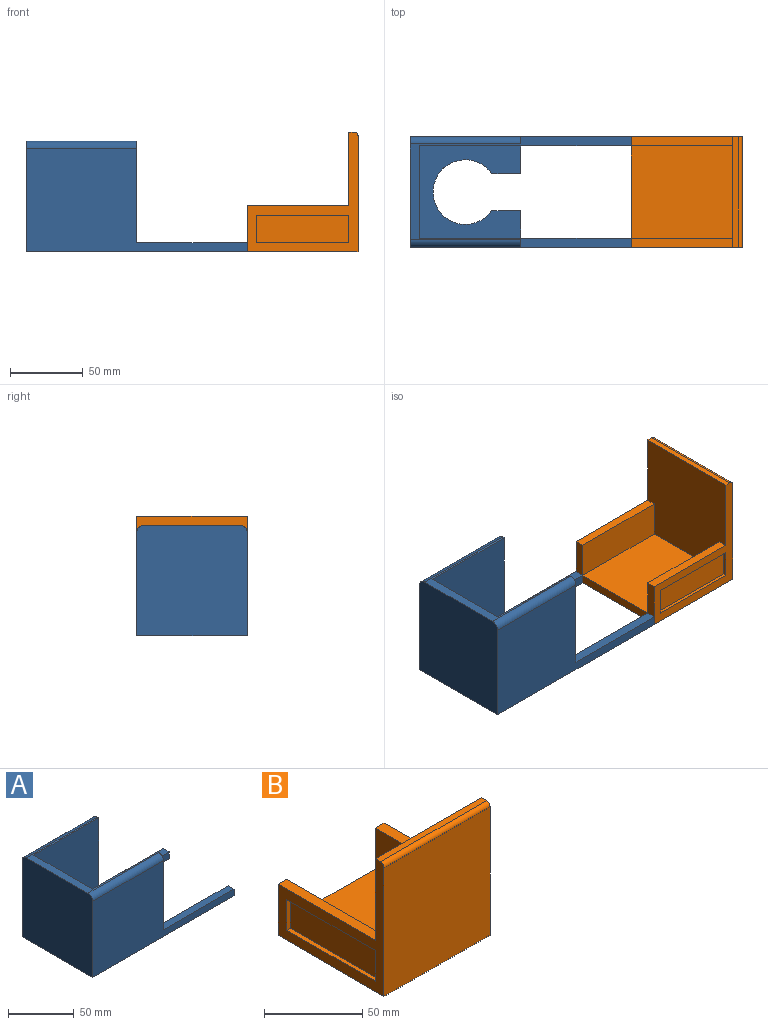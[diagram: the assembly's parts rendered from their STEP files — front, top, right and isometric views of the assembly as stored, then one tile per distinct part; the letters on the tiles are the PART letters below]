
ASSEMBLY  parts=2 mates=1
PART A: 24 faces, bbox 152.4x76.2x76.2 mm
  f0: plane 19.05x6.35mm, normal (1,0,0), area 121mm2, adj f2,f3,f17,f22
  f1: plane 69.85x6.35mm, normal (1,0,0), area 438mm2, adj f7,f9,f12,f15,f18
  f2: plane 69.85x63.5mm, normal (0,0,1), area 2448mm2, adj f0,f6,f9,f10,f11,f13,f16,f17
  f3: plane 152.4x76.2mm, normal (0,0,-1), area 4786.7mm2, adj f0,f5,f6,f7,f8,f13,f16,f17
  f4: plane 69.85x6.35mm, normal (1,0,0), area 438mm2, adj f8,f11,f12,f14,f21
  f5: plane 76.2x76.2mm, normal (-1,0,0), area 5795.4mm2, adj f3,f7,f8,f12,f14,f15
  f6: plane 19.05x6.35mm, normal (1,0,0), area 121mm2, adj f2,f3,f16,f19
  f7: plane 152.4x71.12mm, normal (0,-1,0), area 5903.2mm2, adj f1,f3,f5,f15,f18,f20
  f8: plane 152.4x71.12mm, normal (0,1,0), area 5903.2mm2, adj f3,f4,f5,f14,f21,f23
  f9: plane 69.85x69.85mm, normal (0,1,0), area 4879mm2, adj f1,f2,f10,f12
  f10: plane 69.85x63.5mm, normal (1,0,0), area 4435.5mm2, adj f2,f9,f11,f12
  f11: plane 69.85x69.85mm, normal (0,-1,0), area 4879mm2, adj f2,f4,f10,f12
  f12: plane 76.2x66.04mm, normal (0,0,1), area 596.8mm2, adj f1,f4,f5,f9,f10,f11,f14,f15
  f13: cylinder r=22.23mm len=44.45mm, axis (0,0,1), area 715.1mm2, adj f2,f3,f16,f17
  f14: cylinder r=5.08mm len=76.2mm, axis (-1,0,0), area 608mm2, adj f4,f5,f8,f12
  f15: cylinder r=5.08mm len=76.2mm, axis (1,0,0), area 608mm2, adj f1,f5,f7,f12
  f16: plane 19.86x6.35mm, normal (0,1,0), area 126.1mm2, adj f2,f3,f6,f13
  f17: plane 19.86x6.35mm, normal (0,-1,0), area 126.1mm2, adj f0,f2,f3,f13
  f18: plane 76.2x6.35mm, normal (0,0,1), area 483.9mm2, adj f1,f7,f19,f20
  f19: plane 76.2x6.35mm, normal (0,1,0), area 483.9mm2, adj f3,f6,f18,f20
  f20: plane 6.35x6.35mm, normal (1,0,0), area 40.3mm2, adj f3,f7,f18,f19
  f21: plane 76.2x6.35mm, normal (0,0,1), area 483.9mm2, adj f4,f8,f22,f23
  f22: plane 76.2x6.35mm, normal (0,-1,0), area 483.9mm2, adj f0,f3,f21,f23
  f23: plane 6.35x6.35mm, normal (1,0,0), area 40.3mm2, adj f3,f8,f21,f22
PART B: 23 faces, bbox 76.2x76.2x82.6 mm
  f0: plane 82.55x76.2mm, normal (-1,0,0), area 1530.9mm2, adj f2,f3,f5,f7,f9,f10,f12,f18
  f1: plane 82.55x76.2mm, normal (1,0,0), area 1530.9mm2, adj f2,f3,f5,f7,f9,f11,f12,f13
  f2: plane 76.2x31.75mm, normal (0,1,0), area 806.5mm2, adj f0,f1,f4,f5,f6,f8,f10,f11
  f3: plane 80.01x76.2mm, normal (0,-1,0), area 6096.8mm2, adj f0,f1,f5,f12
  f4: plane 69.85x63.5mm, normal (0,0,1), area 4435.5mm2, adj f2,f6,f7,f8
  f5: plane 76.2x76.2mm, normal (0,0,-1), area 5806.4mm2, adj f0,f1,f2,f3
  f6: plane 69.85x25.4mm, normal (-1,0,0), area 1774.2mm2, adj f2,f4,f7,f11
  f7: plane 76.2x76.2mm, normal (0,1,0), area 5483.9mm2, adj f0,f1,f4,f6,f8,f9,f10,f11
  f8: plane 69.85x25.4mm, normal (1,0,0), area 1774.2mm2, adj f2,f4,f7,f10
  f9: plane 76.2x3.81mm, normal (0,0,1), area 290.3mm2, adj f0,f1,f7,f12
  f10: plane 69.85x6.35mm, normal (0,0,1), area 443.5mm2, adj f0,f2,f7,f8
  f11: plane 69.85x6.35mm, normal (0,0,1), area 443.5mm2, adj f1,f2,f6,f7
  f12: cylinder r=2.54mm len=76.2mm, axis (-1,0,0), area 304mm2, adj f0,f1,f3,f9
  f13: plane 63.5x2.54mm, normal (0,0,-1), area 161.3mm2, adj f1,f14,f16,f17
  f14: plane 19.05x2.54mm, normal (0,1,0), area 48.4mm2, adj f1,f13,f15,f17
  f15: plane 63.5x2.54mm, normal (0,0,1), area 161.3mm2, adj f1,f14,f16,f17
  f16: plane 19.05x2.54mm, normal (0,-1,0), area 48.4mm2, adj f1,f13,f15,f17
  f17: plane 63.5x19.05mm, normal (1,0,0), area 1209.7mm2, adj f13,f14,f15,f16
  f18: plane 63.5x2.54mm, normal (0,0,-1), area 161.3mm2, adj f0,f19,f21,f22
  f19: plane 19.05x2.54mm, normal (0,-1,0), area 48.4mm2, adj f0,f18,f20,f22
  f20: plane 63.5x2.54mm, normal (0,0,1), area 161.3mm2, adj f0,f19,f21,f22
  f21: plane 19.05x2.54mm, normal (0,1,0), area 48.4mm2, adj f0,f18,f20,f22
  f22: plane 63.5x19.05mm, normal (-1,0,0), area 1209.7mm2, adj f18,f19,f20,f21
PLACE A t=(201.11,190.34,201.98)mm
PLACE B rot(axis=(0,0,1),90deg) t=(390.24,150.27,199.85)mm
MATE fastened A.f20 <-> B.f2  axis (1,0,0) through (346.76,114.14,199.85)mm
